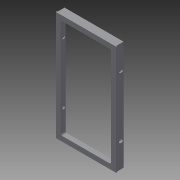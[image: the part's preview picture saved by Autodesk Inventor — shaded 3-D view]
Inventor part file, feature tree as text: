
AUTODESK INVENTOR PART (.ipt)
format: ipt  version: 2015 (Build 190159000, 159)  size: 182,272 bytes
history: native  units: mm
features: extrude x4, sketch x3
ambient origin geometry x8: Origin, YZ Plane, XZ Plane, XY Plane, X Axis, Y Axis, Z Axis, Center Point
bodies: Solid1 (feature_tree)
feature tree (7):
  extrude  "Extrusion1"  Depth=9.0mm TaperAngle=0.0deg
  extrude  "Extrusion5"  Depth=4.0mm
  extrude  "Extrusion6"  Depth=7.5mm
  extrude  "Extrusion7"  Depth=7.5mm
  sketch  "Sketch5"  dims[d0=4.0mm d2=4.0mm d8=9.0mm d9=0.0mm]
  sketch  "Sketch6"  dims[d10=4.0mm d43=4.0mm d51=8.852mm d54=4.0mm d67=8.0mm]
  sketch  "Sketch7"  dims[d77=57.15mm d78=3.81mm d79=3.81mm d80=3.81mm d81=3.81mm d82=3.0mm d85=111.76mm d88=3.81mm d99=1.0mm d100=0.5mm d101=5.0mm d103=1.0mm d104=0.5mm d107=5.0mm d109=5.0mm d111=5.0mm d115=0.5mm d116=5.0mm d121=1.0mm d122=5.0mm d123=2.0mm d129=0.5mm d130=2.0mm d131=1.9mm d132=7.0mm d133=0.0mm d134=2.0mm d135=1.9mm d136=1.9mm d137=1.9mm d138=63.35mm d139=3.0mm d140=7.0mm d141=5.5mm d142=27.0mm d143=27.0mm d144=70.0mm d145=0.0mm d146=3.0mm d147=3.0mm d148=1.5mm d149=1.5mm d150=0.7mm d151=0.7mm d152=7.5mm d153=0.0mm]
